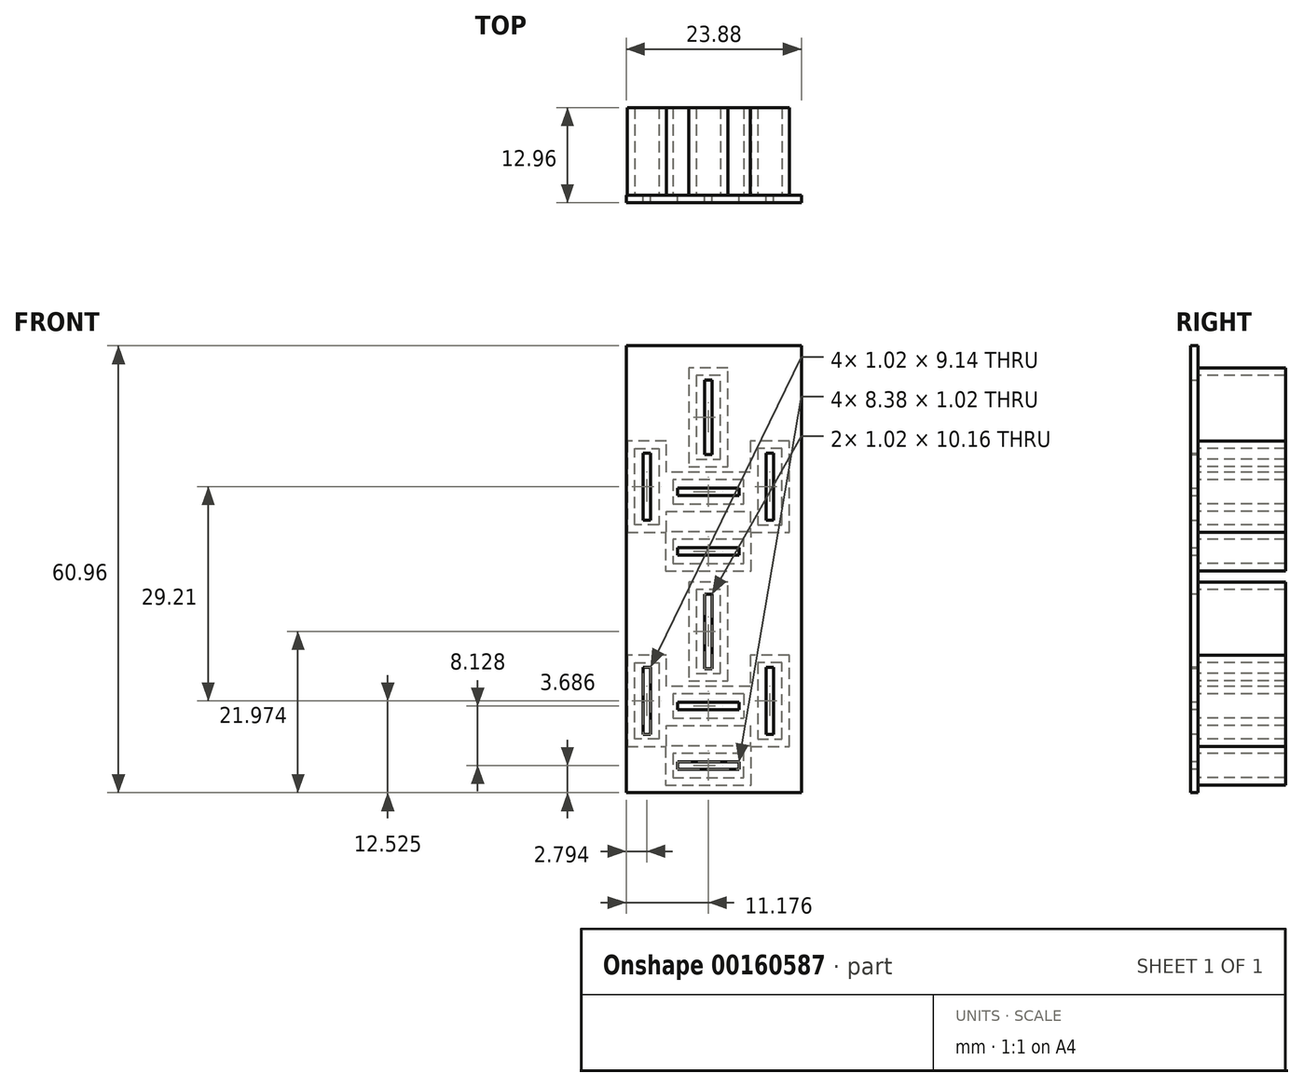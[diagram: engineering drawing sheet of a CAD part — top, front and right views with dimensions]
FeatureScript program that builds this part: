
annotation { "Feature Type Name" : "Feature", "Feature Type Description" : "" }
export const myFeature = defineFeature(function(context is Context, id is Id, definition is map)
    precondition{}
    {
        {
            var Q0;
            Q0=qCreatedBy(makeId("Front.planeOp"),FACE);
            var sketch = newSketch(context, id + "F0", { "sketchPlane" : qUnion([Q0])});
            skLineSegment(sketch, "E0", {"start": v(-3.35, 4.3) * mm, "end": v(-3.35, -26.19) * mm});
            skLineSegment(sketch, "E1", {"start": v(-3.35, -26.19) * mm, "end": v(22.05, -26.19) * mm});
            skLineSegment(sketch, "E2", {"start": v(22.05, -26.19) * mm, "end": v(22.05, 4.3) * mm});
            skLineSegment(sketch, "E3", {"start": v(22.05, 4.3) * mm, "end": v(-3.35, 4.3) * mm});
            skSolve(sketch);
        }
        {
            var Q0;
            Q0=qSketchRegion(id+"F0",true);
            extrude(context, id + "F1", {"entities" : qUnion([Q0]), "depth" : 1.02 * mm});
        }
        {
            var Q0;
            Q0=qCreatedBy(makeId("Front.planeOp"),FACE);
            var sketch = newSketch(context, id + "F2", { "sketchPlane" : qUnion([Q0])});
            skLineSegment(sketch, "E4", {"start": v(8.84, -0.4) * mm, "end": v(8.84, -10.57) * mm});
            skLineSegment(sketch, "E5", {"start": v(8.84, -10.57) * mm, "end": v(9.85, -10.57) * mm});
            skLineSegment(sketch, "E6", {"start": v(9.85, -10.57) * mm, "end": v(9.85, -0.4) * mm});
            skLineSegment(sketch, "E7", {"start": v(9.85, -0.4) * mm, "end": v(8.84, -0.4) * mm});
            skLineSegment(sketch, "E8", {"start": v(0.46, -10.36) * mm, "end": v(0.46, -19.5) * mm});
            skLineSegment(sketch, "E9", {"start": v(0.46, -19.5) * mm, "end": v(1.47, -19.5) * mm});
            skLineSegment(sketch, "E10", {"start": v(1.47, -19.5) * mm, "end": v(1.47, -10.36) * mm});
            skLineSegment(sketch, "E11", {"start": v(1.47, -10.36) * mm, "end": v(0.46, -10.36) * mm});
            skLineSegment(sketch, "E12", {"start": v(17.22, -10.36) * mm, "end": v(17.22, -19.5) * mm});
            skLineSegment(sketch, "E13", {"start": v(17.22, -19.5) * mm, "end": v(18.24, -19.5) * mm});
            skLineSegment(sketch, "E14", {"start": v(18.24, -19.5) * mm, "end": v(18.24, -10.36) * mm});
            skLineSegment(sketch, "E15", {"start": v(17.22, -10.36) * mm, "end": v(18.24, -10.36) * mm});
            skLineSegment(sketch, "E16", {"start": v(5.15, -15.14) * mm, "end": v(5.15, -16.15) * mm});
            skLineSegment(sketch, "E17", {"start": v(5.15, -16.15) * mm, "end": v(13.54, -16.15) * mm});
            skLineSegment(sketch, "E18", {"start": v(13.54, -16.15) * mm, "end": v(13.54, -15.14) * mm});
            skLineSegment(sketch, "E19", {"start": v(5.15, -15.14) * mm, "end": v(13.54, -15.14) * mm});
            skLineSegment(sketch, "E20", {"start": v(5.15, -24.28) * mm, "end": v(13.54, -24.28) * mm});
            skLineSegment(sketch, "E21", {"start": v(13.54, -24.28) * mm, "end": v(13.54, -23.27) * mm});
            skLineSegment(sketch, "E22", {"start": v(13.54, -23.27) * mm, "end": v(5.15, -23.27) * mm});
            skLineSegment(sketch, "E23", {"start": v(5.15, -23.27) * mm, "end": v(5.15, -24.28) * mm});
            skSolve(sketch);
        }
        {
            var Q0;
            Q0=qSketchRegion(id+"F2",true);
            extrude(context, id + "F3", {"entities" : qUnion([Q0]), "operationType" : NewBodyOperationType.REMOVE, "endBound" : BoundingType.THROUGH_ALL, "depth" : 25.4 * mm});
        }
        {
            var Q0;
            Q0=makeQuery(id+"F1.opExtrude","CAP_FACE",FACE,{"disambiguationData":[OSD([sQuery(id+"F0.wireOp",EDGE,"E0"),sQuery(id+"F0.wireOp",EDGE,"E1"),sQuery(id+"F0.wireOp",EDGE,"E2"),sQuery(id+"F0.wireOp",EDGE,"E3")])],"isStart":false});
            var sketch = newSketch(context, id + "F4", { "sketchPlane" : qUnion([Q0])});
            skLineSegment(sketch, "E24", {"start": v(-3.35, -26.19) * mm, "end": v(-3.35, -56.67) * mm});
            skLineSegment(sketch, "E25", {"start": v(-3.35, -56.67) * mm, "end": v(22.05, -56.67) * mm});
            skLineSegment(sketch, "E26", {"start": v(22.05, -56.67) * mm, "end": v(22.05, -26.19) * mm});
            skLineSegment(sketch, "E27", {"start": v(-3.35, -26.19) * mm, "end": v(22.05, -26.19) * mm});
            skSolve(sketch);
        }
        {
            var Q0;
            Q0=qSketchRegion(id+"F4",true);
            extrude(context, id + "F5", {"entities" : qUnion([Q0]), "operationType" : NewBodyOperationType.ADD, "oppositeDirection" : true, "depth" : 1.02 * mm});
        }
        {
            var Q0;
            Q0=makeQuery(id+"F5.boolean.opBoolean","MERGE",FACE,{"derivedFrom":[makeQuery(id+"F1.opExtrude","CAP_FACE",FACE,{"disambiguationData":[OSD([sQuery(id+"F0.wireOp",EDGE,"E0"),sQuery(id+"F0.wireOp",EDGE,"E1"),sQuery(id+"F0.wireOp",EDGE,"E2"),sQuery(id+"F0.wireOp",EDGE,"E3")])],"isStart":false}),makeQuery(id+"F5.opExtrude","CAP_FACE",FACE,{"disambiguationData":[OSD([sQuery(id+"F4.wireOp",EDGE,"E24"),sQuery(id+"F4.wireOp",EDGE,"E25"),sQuery(id+"F4.wireOp",EDGE,"E26"),sQuery(id+"F4.wireOp",EDGE,"E27")])],"isStart":true})]});
            var sketch = newSketch(context, id + "F6", { "sketchPlane" : qUnion([Q0])});
            skLineSegment(sketch, "E28", {"start": v(1.47, -10.36) * mm, "end": v(0.46, -10.36) * mm});
            skLineSegment(sketch, "E29", {"start": v(0.46, -10.36) * mm, "end": v(0.46, -19.5) * mm});
            skLineSegment(sketch, "E30", {"start": v(0.46, -19.5) * mm, "end": v(1.47, -19.5) * mm});
            skLineSegment(sketch, "E31", {"start": v(1.47, -19.5) * mm, "end": v(1.47, -10.36) * mm});
            skLineSegment(sketch, "E32", {"start": v(5.15, -15.14) * mm, "end": v(5.15, -16.15) * mm});
            skLineSegment(sketch, "E33", {"start": v(5.15, -16.15) * mm, "end": v(13.54, -16.15) * mm});
            skLineSegment(sketch, "E34", {"start": v(13.54, -16.15) * mm, "end": v(13.54, -15.14) * mm});
            skLineSegment(sketch, "E35", {"start": v(13.54, -15.14) * mm, "end": v(5.15, -15.14) * mm});
            skLineSegment(sketch, "E36", {"start": v(8.84, -10.57) * mm, "end": v(9.85, -10.57) * mm});
            skLineSegment(sketch, "E37", {"start": v(9.85, -10.57) * mm, "end": v(9.85, -0.4) * mm});
            skLineSegment(sketch, "E38", {"start": v(9.85, -0.4) * mm, "end": v(8.84, -0.4) * mm});
            skLineSegment(sketch, "E39", {"start": v(8.84, -0.4) * mm, "end": v(8.84, -10.57) * mm});
            skLineSegment(sketch, "E40", {"start": v(17.22, -10.36) * mm, "end": v(18.24, -10.36) * mm});
            skLineSegment(sketch, "E41", {"start": v(18.24, -10.36) * mm, "end": v(18.24, -19.5) * mm});
            skLineSegment(sketch, "E42", {"start": v(18.24, -19.5) * mm, "end": v(17.22, -19.5) * mm});
            skLineSegment(sketch, "E43", {"start": v(17.22, -19.5) * mm, "end": v(17.22, -10.36) * mm});
            skLineSegment(sketch, "E44", {"start": v(13.54, -23.27) * mm, "end": v(13.54, -24.28) * mm});
            skLineSegment(sketch, "E45", {"start": v(13.54, -24.28) * mm, "end": v(5.15, -24.28) * mm});
            skLineSegment(sketch, "E46", {"start": v(5.15, -24.28) * mm, "end": v(5.15, -23.27) * mm});
            skLineSegment(sketch, "E47", {"start": v(5.15, -23.27) * mm, "end": v(13.54, -23.27) * mm});
            skLineSegment(sketch, "E48.0.1.0", {"start": v(9.85, -39.78) * mm, "end": v(9.85, -29.62) * mm});
            skLineSegment(sketch, "E48.0.1.1", {"start": v(8.84, -29.62) * mm, "end": v(8.84, -39.78) * mm});
            skLineSegment(sketch, "E48.0.1.2", {"start": v(17.22, -48.72) * mm, "end": v(17.22, -39.57) * mm});
            skLineSegment(sketch, "E48.0.1.3", {"start": v(18.24, -39.57) * mm, "end": v(18.24, -48.72) * mm});
            skLineSegment(sketch, "E48.0.1.4", {"start": v(13.54, -44.35) * mm, "end": v(5.15, -44.35) * mm});
            skLineSegment(sketch, "E48.0.1.5", {"start": v(5.15, -45.36) * mm, "end": v(13.54, -45.36) * mm});
            skLineSegment(sketch, "E48.0.1.6", {"start": v(5.15, -52.48) * mm, "end": v(13.54, -52.48) * mm});
            skLineSegment(sketch, "E48.0.1.7", {"start": v(13.54, -53.5) * mm, "end": v(5.15, -53.5) * mm});
            skLineSegment(sketch, "E48.0.1.8", {"start": v(1.47, -48.72) * mm, "end": v(1.47, -39.57) * mm});
            skLineSegment(sketch, "E48.0.1.9", {"start": v(0.46, -39.57) * mm, "end": v(0.46, -48.72) * mm});
            skLineSegment(sketch, "E48.0.1.10", {"start": v(1.47, -39.57) * mm, "end": v(0.46, -39.57) * mm});
            skLineSegment(sketch, "E48.0.1.11", {"start": v(0.46, -48.72) * mm, "end": v(1.47, -48.72) * mm});
            skLineSegment(sketch, "E48.0.1.12", {"start": v(5.15, -44.35) * mm, "end": v(5.15, -45.36) * mm});
            skLineSegment(sketch, "E48.0.1.13", {"start": v(13.54, -45.36) * mm, "end": v(13.54, -44.35) * mm});
            skLineSegment(sketch, "E48.0.1.14", {"start": v(17.22, -39.57) * mm, "end": v(18.24, -39.57) * mm});
            skLineSegment(sketch, "E48.0.1.15", {"start": v(18.24, -48.72) * mm, "end": v(17.22, -48.72) * mm});
            skLineSegment(sketch, "E48.0.1.16", {"start": v(8.84, -39.78) * mm, "end": v(9.85, -39.78) * mm});
            skLineSegment(sketch, "E48.0.1.17", {"start": v(9.85, -29.62) * mm, "end": v(8.84, -29.62) * mm});
            skLineSegment(sketch, "E48.0.1.18", {"start": v(5.15, -53.5) * mm, "end": v(5.15, -52.48) * mm});
            skLineSegment(sketch, "E48.0.1.19", {"start": v(13.54, -52.48) * mm, "end": v(13.54, -53.5) * mm});
            skLineSegment(sketch, "E48.direction1", {"start": v(9.85, -10.57) * mm, "end": v(35.25, -10.57) * mm, "construction": true});
            skLineSegment(sketch, "E48.direction2", {"start": v(9.85, -10.57) * mm, "end": v(9.85, -39.78) * mm, "construction": true});
            skSolve(sketch);
        }
        {
            var Q0;
            Q0=qSketchRegion(id+"F6",true);
            extrude(context, id + "F7", {"entities" : qUnion([Q0]), "operationType" : NewBodyOperationType.REMOVE, "endBound" : BoundingType.THROUGH_ALL, "oppositeDirection" : true, "depth" : 25.4 * mm});
        }
        {
            var Q0;
            Q0=makeQuery(id+"F5.boolean.opBoolean","MERGE",FACE,{"derivedFrom":[makeQuery(id+"F1.opExtrude","CAP_FACE",FACE,{"disambiguationData":[OSD([sQuery(id+"F0.wireOp",EDGE,"E0"),sQuery(id+"F0.wireOp",EDGE,"E1"),sQuery(id+"F0.wireOp",EDGE,"E2"),sQuery(id+"F0.wireOp",EDGE,"E3")])],"isStart":false}),makeQuery(id+"F5.opExtrude","CAP_FACE",FACE,{"disambiguationData":[OSD([sQuery(id+"F4.wireOp",EDGE,"E24"),sQuery(id+"F4.wireOp",EDGE,"E25"),sQuery(id+"F4.wireOp",EDGE,"E26"),sQuery(id+"F4.wireOp",EDGE,"E27")])],"isStart":true})]});
            var sketch = newSketch(context, id + "F8", { "sketchPlane" : qUnion([Q0])});
            skLineSegment(sketch, "E49", {"start": v(11, 0.23) * mm, "end": v(7.7, 0.23) * mm});
            skLineSegment(sketch, "E50", {"start": v(7.7, 0.23) * mm, "end": v(7.7, -11.2) * mm});
            skLineSegment(sketch, "E51", {"start": v(7.7, -11.2) * mm, "end": v(11, -11.2) * mm});
            skLineSegment(sketch, "E52", {"start": v(11, -11.2) * mm, "end": v(11, 0.23) * mm});
            skLineSegment(sketch, "E53", {"start": v(-0.69, -9.73) * mm, "end": v(2.61, -9.73) * mm});
            skLineSegment(sketch, "E54", {"start": v(2.61, -9.73) * mm, "end": v(2.61, -20.14) * mm});
            skLineSegment(sketch, "E55", {"start": v(2.61, -20.14) * mm, "end": v(-0.69, -20.14) * mm});
            skLineSegment(sketch, "E56", {"start": v(-0.69, -20.14) * mm, "end": v(-0.69, -9.73) * mm});
            skLineSegment(sketch, "E57", {"start": v(4.52, -22.12) * mm, "end": v(4.52, -25.43) * mm});
            skLineSegment(sketch, "E58", {"start": v(4.52, -25.43) * mm, "end": v(14.17, -25.43) * mm});
            skLineSegment(sketch, "E59", {"start": v(14.17, -25.43) * mm, "end": v(14.17, -22.12) * mm});
            skLineSegment(sketch, "E60", {"start": v(14.17, -22.12) * mm, "end": v(4.52, -22.12) * mm});
            skLineSegment(sketch, "E61", {"start": v(16.08, -9.73) * mm, "end": v(16.08, -20.14) * mm});
            skLineSegment(sketch, "E62", {"start": v(16.08, -20.14) * mm, "end": v(19.38, -20.14) * mm});
            skLineSegment(sketch, "E63", {"start": v(19.38, -20.14) * mm, "end": v(19.38, -9.73) * mm});
            skLineSegment(sketch, "E64", {"start": v(19.38, -9.73) * mm, "end": v(16.08, -9.73) * mm});
            skLineSegment(sketch, "E65", {"start": v(4.52, -14) * mm, "end": v(4.52, -17.3) * mm});
            skLineSegment(sketch, "E66", {"start": v(4.52, -17.3) * mm, "end": v(14.17, -17.3) * mm});
            skLineSegment(sketch, "E67", {"start": v(14.17, -17.3) * mm, "end": v(14.17, -14) * mm});
            skLineSegment(sketch, "E68", {"start": v(14.17, -14) * mm, "end": v(4.52, -14) * mm});
            skLineSegment(sketch, "E69", {"start": v(6.68, 1.24) * mm, "end": v(6.68, -12.22) * mm});
            skLineSegment(sketch, "E70", {"start": v(6.68, -12.22) * mm, "end": v(12.01, -12.22) * mm});
            skLineSegment(sketch, "E71", {"start": v(12.01, -12.22) * mm, "end": v(12.01, 1.24) * mm});
            skLineSegment(sketch, "E72", {"start": v(12.01, 1.24) * mm, "end": v(6.68, 1.24) * mm});
            skLineSegment(sketch, "E73", {"start": v(3.63, -8.71) * mm, "end": v(-1.7, -8.71) * mm});
            skLineSegment(sketch, "E74", {"start": v(-1.7, -8.71) * mm, "end": v(-1.7, -21.16) * mm});
            skLineSegment(sketch, "E75", {"start": v(-1.7, -21.16) * mm, "end": v(3.63, -21.16) * mm});
            skLineSegment(sketch, "E76", {"start": v(3.63, -21.16) * mm, "end": v(3.63, -8.71) * mm});
            skLineSegment(sketch, "E77", {"start": v(3.5, -21.1) * mm, "end": v(3.5, -26.44) * mm});
            skLineSegment(sketch, "E78", {"start": v(3.5, -26.44) * mm, "end": v(15.19, -26.44) * mm});
            skLineSegment(sketch, "E79", {"start": v(15.19, -26.44) * mm, "end": v(15.19, -21.1) * mm});
            skLineSegment(sketch, "E80", {"start": v(15.19, -21.1) * mm, "end": v(3.5, -21.1) * mm});
            skLineSegment(sketch, "E81", {"start": v(15.06, -8.71) * mm, "end": v(15.06, -21.16) * mm});
            skLineSegment(sketch, "E82", {"start": v(15.06, -21.16) * mm, "end": v(20.4, -21.16) * mm});
            skLineSegment(sketch, "E83", {"start": v(20.4, -21.16) * mm, "end": v(20.4, -8.71) * mm});
            skLineSegment(sketch, "E84", {"start": v(20.4, -8.71) * mm, "end": v(15.06, -8.71) * mm});
            skLineSegment(sketch, "E85", {"start": v(3.5, -12.98) * mm, "end": v(3.5, -18.31) * mm});
            skLineSegment(sketch, "E86", {"start": v(3.5, -18.31) * mm, "end": v(15.19, -18.31) * mm});
            skLineSegment(sketch, "E87", {"start": v(15.19, -18.31) * mm, "end": v(15.19, -12.98) * mm});
            skLineSegment(sketch, "E88", {"start": v(15.19, -12.98) * mm, "end": v(3.5, -12.98) * mm});
            skLineSegment(sketch, "E89.0.1.0", {"start": v(12.01, -27.97) * mm, "end": v(6.68, -27.97) * mm});
            skLineSegment(sketch, "E89.0.1.1", {"start": v(11, -28.98) * mm, "end": v(7.7, -28.98) * mm});
            skLineSegment(sketch, "E89.0.1.2", {"start": v(6.68, -27.97) * mm, "end": v(6.68, -41.43) * mm});
            skLineSegment(sketch, "E89.0.1.3", {"start": v(12.01, -41.43) * mm, "end": v(12.01, -27.97) * mm});
            skLineSegment(sketch, "E89.0.1.4", {"start": v(11, -40.41) * mm, "end": v(11, -28.98) * mm});
            skLineSegment(sketch, "E89.0.1.5", {"start": v(7.7, -28.98) * mm, "end": v(7.7, -40.41) * mm});
            skLineSegment(sketch, "E89.0.1.6", {"start": v(7.7, -40.41) * mm, "end": v(11, -40.41) * mm});
            skLineSegment(sketch, "E89.0.1.7", {"start": v(6.68, -41.43) * mm, "end": v(12.01, -41.43) * mm});
            skLineSegment(sketch, "E89.0.1.8", {"start": v(16.08, -38.94) * mm, "end": v(16.08, -49.35) * mm});
            skLineSegment(sketch, "E89.0.1.9", {"start": v(15.06, -37.92) * mm, "end": v(15.06, -50.37) * mm});
            skLineSegment(sketch, "E89.0.1.10", {"start": v(15.06, -50.37) * mm, "end": v(20.4, -50.37) * mm});
            skLineSegment(sketch, "E89.0.1.11", {"start": v(16.08, -49.35) * mm, "end": v(19.38, -49.35) * mm});
            skLineSegment(sketch, "E89.0.1.12", {"start": v(20.4, -50.37) * mm, "end": v(20.4, -37.92) * mm});
            skLineSegment(sketch, "E89.0.1.13", {"start": v(19.38, -49.35) * mm, "end": v(19.38, -38.94) * mm});
            skLineSegment(sketch, "E89.0.1.14", {"start": v(19.38, -38.94) * mm, "end": v(16.08, -38.94) * mm});
            skLineSegment(sketch, "E89.0.1.15", {"start": v(20.4, -37.92) * mm, "end": v(15.06, -37.92) * mm});
            skLineSegment(sketch, "E89.0.1.16", {"start": v(15.19, -42.19) * mm, "end": v(3.5, -42.19) * mm});
            skLineSegment(sketch, "E89.0.1.17", {"start": v(14.17, -43.2) * mm, "end": v(4.52, -43.2) * mm});
            skLineSegment(sketch, "E89.0.1.18", {"start": v(4.52, -46.5) * mm, "end": v(14.17, -46.5) * mm});
            skLineSegment(sketch, "E89.0.1.19", {"start": v(3.5, -47.52) * mm, "end": v(15.19, -47.52) * mm});
            skLineSegment(sketch, "E89.0.1.20", {"start": v(3.5, -42.19) * mm, "end": v(3.5, -47.52) * mm});
            skLineSegment(sketch, "E89.0.1.21", {"start": v(4.52, -43.2) * mm, "end": v(4.52, -46.5) * mm});
            skLineSegment(sketch, "E89.0.1.22", {"start": v(2.61, -38.94) * mm, "end": v(2.61, -49.35) * mm});
            skLineSegment(sketch, "E89.0.1.23", {"start": v(3.63, -50.37) * mm, "end": v(3.63, -37.92) * mm});
            skLineSegment(sketch, "E89.0.1.24", {"start": v(3.63, -37.92) * mm, "end": v(-1.7, -37.92) * mm});
            skLineSegment(sketch, "E89.0.1.25", {"start": v(-1.7, -37.92) * mm, "end": v(-1.7, -50.37) * mm});
            skLineSegment(sketch, "E89.0.1.26", {"start": v(2.61, -49.35) * mm, "end": v(-0.69, -49.35) * mm});
            skLineSegment(sketch, "E89.0.1.27", {"start": v(-0.69, -49.35) * mm, "end": v(-0.69, -38.94) * mm});
            skLineSegment(sketch, "E89.0.1.28", {"start": v(-1.7, -50.37) * mm, "end": v(3.63, -50.37) * mm});
            skLineSegment(sketch, "E89.0.1.29", {"start": v(-0.69, -38.94) * mm, "end": v(2.61, -38.94) * mm});
            skLineSegment(sketch, "E89.0.1.30", {"start": v(15.19, -50.32) * mm, "end": v(3.5, -50.32) * mm});
            skLineSegment(sketch, "E89.0.1.31", {"start": v(14.17, -51.33) * mm, "end": v(4.52, -51.33) * mm});
            skLineSegment(sketch, "E89.0.1.32", {"start": v(3.5, -50.32) * mm, "end": v(3.5, -55.65) * mm});
            skLineSegment(sketch, "E89.0.1.33", {"start": v(4.52, -51.33) * mm, "end": v(4.52, -54.64) * mm});
            skLineSegment(sketch, "E89.0.1.34", {"start": v(3.5, -55.65) * mm, "end": v(15.19, -55.65) * mm});
            skLineSegment(sketch, "E89.0.1.35", {"start": v(4.52, -54.64) * mm, "end": v(14.17, -54.64) * mm});
            skLineSegment(sketch, "E89.0.1.36", {"start": v(14.17, -54.64) * mm, "end": v(14.17, -51.33) * mm});
            skLineSegment(sketch, "E89.0.1.37", {"start": v(15.19, -55.65) * mm, "end": v(15.19, -50.32) * mm});
            skLineSegment(sketch, "E89.direction1", {"start": v(6.68, 1.24) * mm, "end": v(32.08, 1.24) * mm, "construction": true});
            skLineSegment(sketch, "E89.direction2", {"start": v(6.68, 1.24) * mm, "end": v(6.68, -27.97) * mm, "construction": true});
            skLineSegment(sketch, "E90", {"start": v(14.17, -43.2) * mm, "end": v(14.17, -46.5) * mm});
            skLineSegment(sketch, "E91", {"start": v(15.19, -42.19) * mm, "end": v(15.19, -47.52) * mm});
            skSolve(sketch);
        }
        {
            var Q0;
            Q0=qSketchRegion(id+"F8",true);
            extrude(context, id + "F9", {"entities" : qUnion([Q0]), "operationType" : NewBodyOperationType.ADD, "oppositeDirection" : true, "depth" : 12.95 * mm});
        }
        {
            var Q0;
            Q0=makeQuery(id+"F5.boolean.opBoolean","MERGE",FACE,{"derivedFrom":[makeQuery(id+"F1.opExtrude","CAP_FACE",FACE,{"disambiguationData":[OSD([sQuery(id+"F0.wireOp",EDGE,"E0"),sQuery(id+"F0.wireOp",EDGE,"E1"),sQuery(id+"F0.wireOp",EDGE,"E2"),sQuery(id+"F0.wireOp",EDGE,"E3")])],"isStart":false}),makeQuery(id+"F5.opExtrude","CAP_FACE",FACE,{"disambiguationData":[OSD([sQuery(id+"F4.wireOp",EDGE,"E24"),sQuery(id+"F4.wireOp",EDGE,"E25"),sQuery(id+"F4.wireOp",EDGE,"E26"),sQuery(id+"F4.wireOp",EDGE,"E27")])],"isStart":true})]});
            var sketch = newSketch(context, id + "F10", { "sketchPlane" : qUnion([Q0])});
            skLineSegment(sketch, "E92", {"start": v(-3.35, 4.3) * mm, "end": v(-1.83, 4.3) * mm});
            skLineSegment(sketch, "E93", {"start": v(-1.83, 4.3) * mm, "end": v(-1.83, -56.67) * mm});
            skLineSegment(sketch, "E94", {"start": v(-1.83, -56.67) * mm, "end": v(-3.35, -56.67) * mm});
            skLineSegment(sketch, "E95", {"start": v(-3.35, -56.67) * mm, "end": v(-3.35, 4.3) * mm});
            skSolve(sketch);
        }
        {
            var Q0;
            Q0=qSketchRegion(id+"F10",true);
            extrude(context, id + "F11", {"entities" : qUnion([Q0]), "operationType" : NewBodyOperationType.REMOVE, "oppositeDirection" : true, "depth" : 25.4 * mm});
        }
    });
